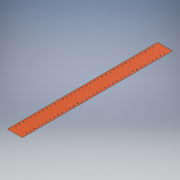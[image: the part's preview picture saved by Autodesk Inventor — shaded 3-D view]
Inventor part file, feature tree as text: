
AUTODESK INVENTOR PART (.ipt)
format: ipt  version: 2019 (Build 230136000, 136)  size: 241,152 bytes
history: native  units: mm
features: extrude x2, other x2, mirror x1
ambient origin geometry x8: Origin, YZ Plane, XZ Plane, XY Plane, X Axis, Y Axis, Z Axis, Center Point
bodies: Body1 (feature_tree)
feature tree (5):
  extrude  "Skin Body"  Depth=1819.0mm
  extrude  "End Cut"  Depth=909.5mm
  mirror  "End Cut Mirror"
  other  "Skin Scheme"
  other  "End Cut Outline"
